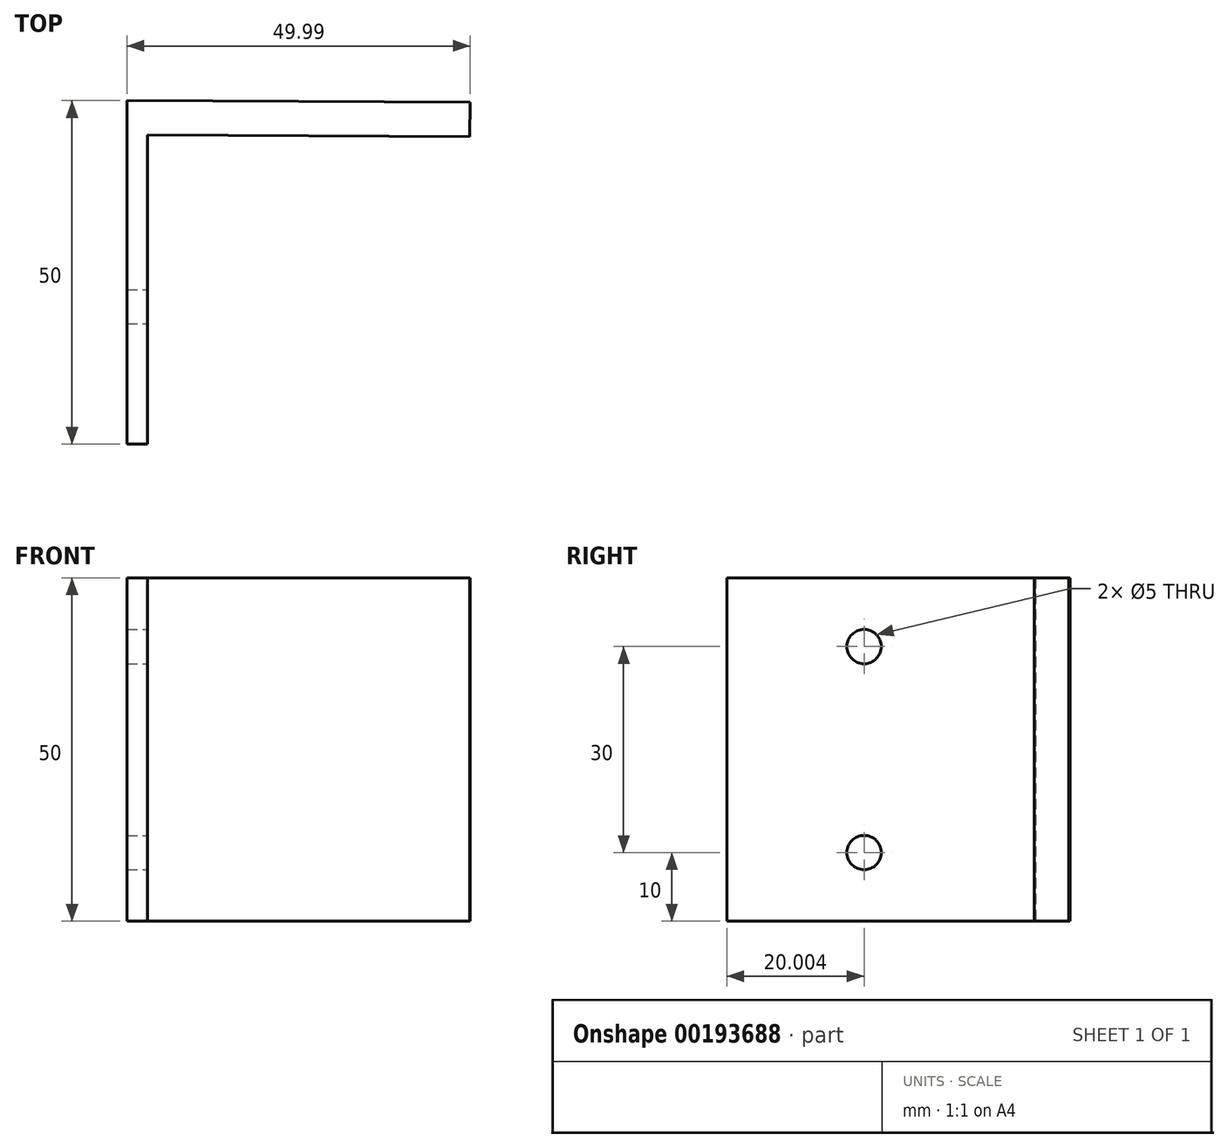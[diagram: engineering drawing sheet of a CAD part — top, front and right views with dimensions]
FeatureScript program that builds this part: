
annotation { "Feature Type Name" : "Feature", "Feature Type Description" : "" }
export const myFeature = defineFeature(function(context is Context, id is Id, definition is map)
    precondition{}
    {
        {
            var Q0;
            Q0=qCreatedBy(makeId("Top.planeOp"),FACE);
            var sketch = newSketch(context, id + "F0", { "sketchPlane" : qUnion([Q0])});
            skLineSegment(sketch, "E0", {"start": v(-54.4, 7.94) * mm, "end": v(-54.4, -42.06) * mm});
            skLineSegment(sketch, "E1", {"start": v(-54.4, -42.06) * mm, "end": v(-51.4, -42.06) * mm});
            skLineSegment(sketch, "E2", {"start": v(-51.4, -42.06) * mm, "end": v(-51.4, 2.94) * mm});
            skLineSegment(sketch, "E3", {"start": v(-4.4, 7.72) * mm, "end": v(-54.4, 7.94) * mm});
            skPoint(sketch, "E4.end.orphan", {"position": v(-6.4, 5.94) * mm});
            skPoint(sketch, "E5.end.orphan", {"position": v(-6.4, 2.94) * mm});
            skLineSegment(sketch, "E6", {"start": v(-51.4, 2.94) * mm, "end": v(-4.52, 2.73) * mm});
            skLineSegment(sketch, "E7", {"start": v(-4.52, 2.73) * mm, "end": v(-4.4, 7.72) * mm});
            skSolve(sketch);
        }
        {
            var Q0;
            Q0=makeQuery(id+"F0.imprint","IMPRINT",FACE,{"disambiguationData":[TD([[makeQuery(id+"F0.imprint","IMPRINT",EDGE,{"derivedFrom":sQuery(id+"F0.wireOp",EDGE,"E0")}),1.0]])]});
            extrude(context, id + "F1", {"entities" : qUnion([Q0]), "depth" : 50 * mm});
        }
        {
            var Q0;
            Q0=qCreatedBy(makeId("Right.planeOp"),FACE);
            var sketch = newSketch(context, id + "F2", { "sketchPlane" : qUnion([Q0])});
            skCircle(sketch, "E8", {"center": v(-22.06, 40) * mm, "radius": 2.5 * mm});
            skCircle(sketch, "E9", {"center": v(-22.06, 10) * mm, "radius": 2.5 * mm});
            skSolve(sketch);
        }
        {
            var Q0;
            Q0 = qSketchRegion(id + "F2", true);
            extrude(context, id + "F3", {"entities" : qUnion([Q0]), "operationType" : NewBodyOperationType.REMOVE, "oppositeDirection" : true, "depth" : 93 * mm});
        }
    });
